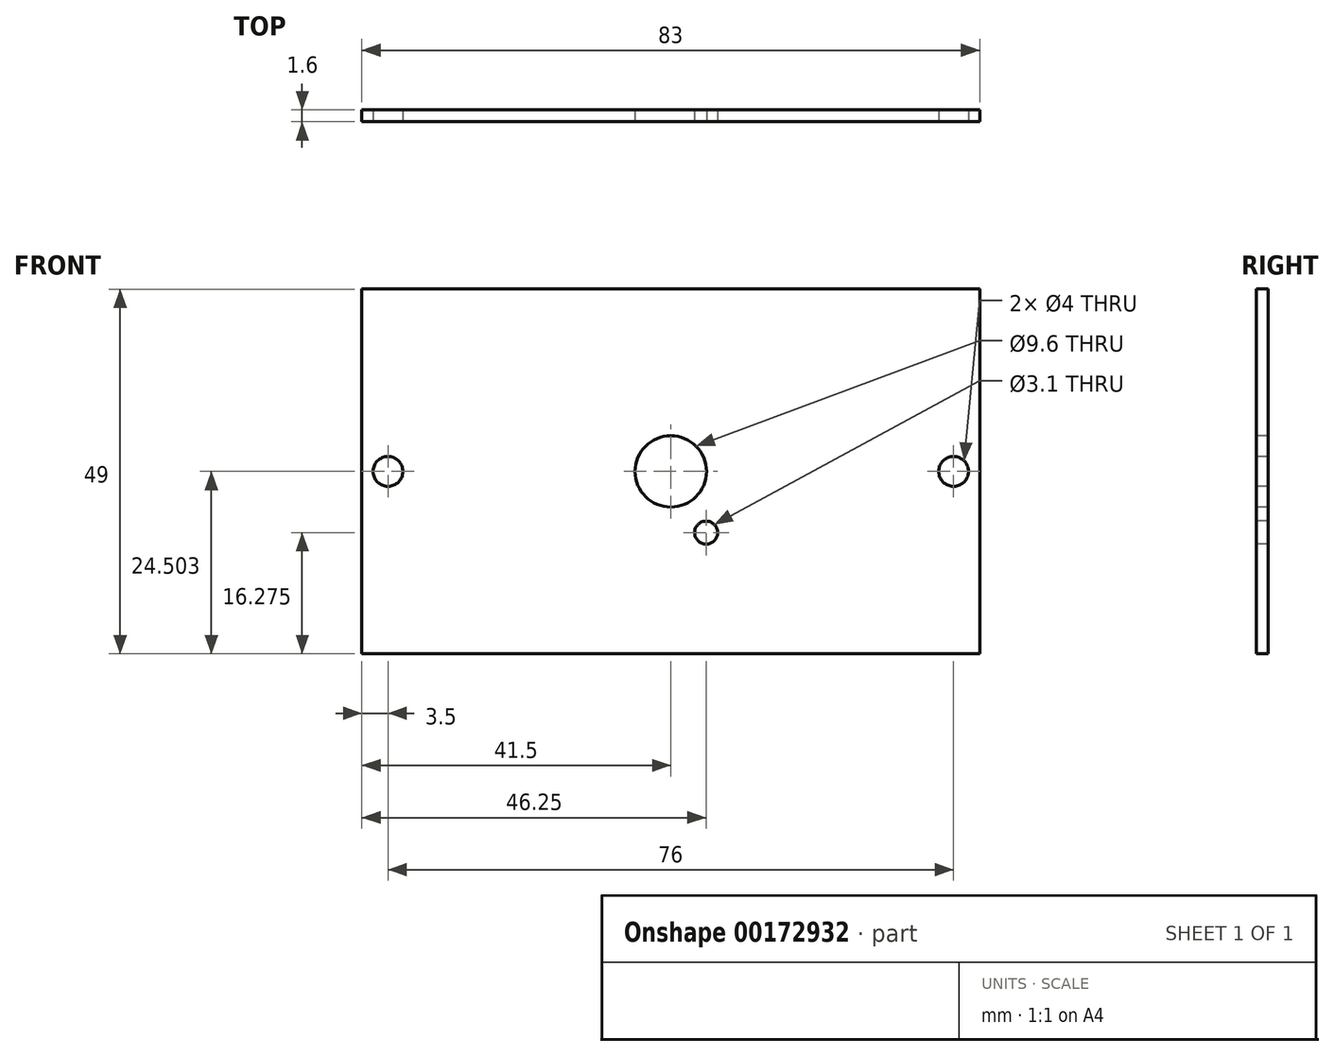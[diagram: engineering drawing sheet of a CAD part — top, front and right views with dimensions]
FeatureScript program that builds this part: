
annotation { "Feature Type Name" : "Feature", "Feature Type Description" : "" }
export const myFeature = defineFeature(function(context is Context, id is Id, definition is map)
    precondition{}
    {
        {
            var Q0;
            Q0=qCreatedBy(makeId("Front.planeOp"),FACE);
            var sketch = newSketch(context, id + "F0", { "sketchPlane" : qUnion([Q0])});
            skLineSegment(sketch, "E0.bottom", {"start": v(41.5, 20.97) * mm, "end": v(-41.5, 20.97) * mm});
            skLineSegment(sketch, "E0.top", {"start": v(41.5, -28.03) * mm, "end": v(-41.5, -28.03) * mm});
            skLineSegment(sketch, "E0.left", {"start": v(41.5, 20.97) * mm, "end": v(41.5, -28.03) * mm});
            skLineSegment(sketch, "E0.right", {"start": v(-41.5, 20.97) * mm, "end": v(-41.5, -28.03) * mm});
            skPoint(sketch, "E0.middle", {"position": v(0, -3.53) * mm});
            skSolve(sketch);
        }
        {
            var Q0;
            Q0=qSketchRegion(id+"F0",true);
            extrude(context, id + "F1", {"entities" : qUnion([Q0]), "oppositeDirection" : true, "depth" : 1.6 * mm});
        }
        {
            var Q0;
            Q0=makeQuery(id+"F1.opExtrude","CAP_FACE",FACE,{"disambiguationData":[OSD([sQuery(id+"F0.wireOp",EDGE,"E0.bottom"),sQuery(id+"F0.wireOp",EDGE,"E0.top"),sQuery(id+"F0.wireOp",EDGE,"E0.left"),sQuery(id+"F0.wireOp",EDGE,"E0.right")])],"isStart":true});
            var sketch = newSketch(context, id + "F2", { "sketchPlane" : qUnion([Q0])});
            skPoint(sketch, "E1", {"position": v(-38, -3.53) * mm});
            skPoint(sketch, "E2", {"position": v(38, -3.53) * mm});
            skPoint(sketch, "E3", {"position": v(0, -3.53) * mm});
            skLineSegment(sketch, "E4", {"start": v(0, 20.38) * mm, "end": v(0, -28.03) * mm, "construction": true});
            skPoint(sketch, "E4.startSnap0", {"position": v(0, 20.97) * mm});
            skPoint(sketch, "E5", {"position": v(4.75, -11.75) * mm});
            skLineSegment(sketch, "E6", {"start": v(0, -3.53) * mm, "end": v(7.14, -15.9) * mm, "construction": true});
            skLineSegment(sketch, "E7", {"start": v(0, -3.53) * mm, "end": v(0, -28.03) * mm, "construction": true});
            skSolve(sketch);
        }
        {
            var Q0;
            Q0=sQuery(id+"F2.wireOp",VERTEX,"E1");
            var Q1;
            Q1=sQuery(id+"F2.wireOp",VERTEX,"E2");
            var Q2;
            Q2=makeQuery(id+"F1.opExtrude","SWEPT_BODY",BODY,{"disambiguationData":[OSD([sQuery(id+"F0.wireOp",EDGE,"E0.bottom"),sQuery(id+"F0.wireOp",EDGE,"E0.top"),sQuery(id+"F0.wireOp",EDGE,"E0.left"),sQuery(id+"F0.wireOp",EDGE,"E0.right")])]});
            hole(context, id + "F3", {"style" : HoleStyle.SIMPLE, "endStyle" : HoleEndStyle.THROUGH, "holeDiameter" : 4 * mm, "locations" : qUnion([Q0, Q1]), "scope" : qUnion([Q2]), "isTappedThrough" : true});
        }
        {
            var Q0;
            Q0=sQuery(id+"F2.wireOp",VERTEX,"E3");
            var Q1;
            Q1=makeQuery(id+"F1.opExtrude","SWEPT_BODY",BODY,{"disambiguationData":[OSD([sQuery(id+"F0.wireOp",EDGE,"E0.bottom"),sQuery(id+"F0.wireOp",EDGE,"E0.top"),sQuery(id+"F0.wireOp",EDGE,"E0.left"),sQuery(id+"F0.wireOp",EDGE,"E0.right")])]});
            hole(context, id + "F4", {"style" : HoleStyle.SIMPLE, "endStyle" : HoleEndStyle.THROUGH, "holeDiameter" : 9.6 * mm, "locations" : qUnion([Q0]), "scope" : qUnion([Q1]), "isTappedThrough" : true});
        }
        {
            var Q0;
            Q0=sQuery(id+"F2.wireOp",VERTEX,"E5");
            var Q1;
            Q1=makeQuery(id+"F1.opExtrude","SWEPT_BODY",BODY,{"disambiguationData":[OSD([sQuery(id+"F0.wireOp",EDGE,"E0.bottom"),sQuery(id+"F0.wireOp",EDGE,"E0.top"),sQuery(id+"F0.wireOp",EDGE,"E0.left"),sQuery(id+"F0.wireOp",EDGE,"E0.right")])]});
            hole(context, id + "F5", {"style" : HoleStyle.SIMPLE, "endStyle" : HoleEndStyle.THROUGH, "holeDiameter" : 3.1 * mm, "locations" : qUnion([Q0]), "scope" : qUnion([Q1]), "isTappedThrough" : true});
        }
    });
